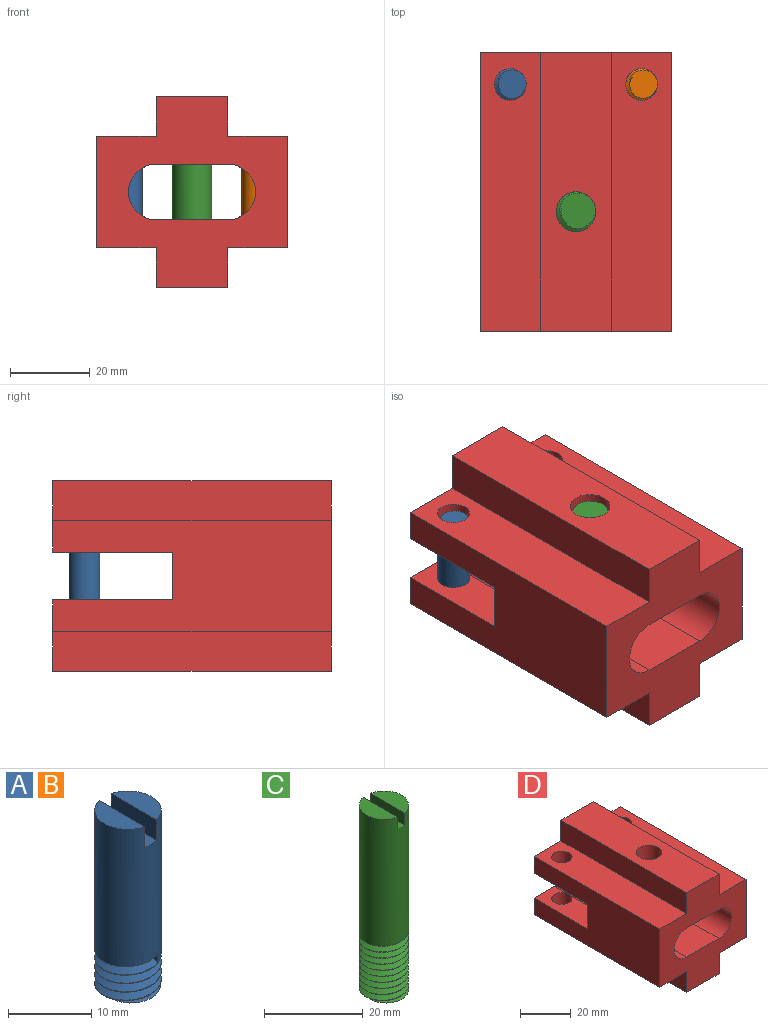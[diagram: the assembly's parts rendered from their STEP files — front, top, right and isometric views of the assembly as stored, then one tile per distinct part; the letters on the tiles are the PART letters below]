
ASSEMBLY  parts=4 mates=3
PART A: 14 faces, bbox 8.7x9.9x27.3 mm
  f0: cylinder r=4mm len=22.25mm, axis (0,0,1), area 508.2mm2, adj f1,f5,f7,f8,f9,f10,f11,f12
  f1: cylinder r=4mm len=8mm, axis (0,0,1), area 2.5mm2, adj f0,f2,f8,f9
  f2: cylinder r=4mm len=8mm, axis (0,0,1), area 2.5mm2, adj f1,f3,f8,f9
  f3: cylinder r=4mm len=8mm, axis (0,0,1), area 2.5mm2, adj f2,f4,f8,f9
  f4: cylinder r=4mm len=1.78mm, axis (0,0,1), area 0.1mm2, adj f3,f6,f9
  f5: plane 7.75x3mm, normal (0,0,1), area 17.2mm2, adj f0,f12
  f6: plane 7.82x7.8mm, normal (0,0,-1), area 39.7mm2, adj f4,f8,f9
  f7: plane 7.75x3mm, normal (0,0,1), area 17.2mm2, adj f0,f11
  f8: bspline ~9.24x8mm, area 116.1mm2, adj f0,f1,f2,f3,f6,f9,f10
  f9: bspline ~8.01x7.99mm, area 104mm2, adj f0,f1,f2,f3,f4,f6,f8,f10
  f10: plane 1.15x0.96mm, normal (-0.95,-0.31,-0.05), area 0.6mm2, adj f0,f8,f9
  f11: plane 7.75x3mm, normal (1,0,0), area 23.2mm2, adj f0,f7,f13
  f12: plane 7.75x3mm, normal (-1,0,0), area 23.2mm2, adj f0,f5,f13
  f13: plane 8x2mm, normal (0,0,1), area 15.8mm2, adj f0,f11,f12
PART B: same geometry as A
PART C: 21 faces, bbox 10.1x11.6x46.8 mm
  f0: cylinder r=5mm len=32.41mm, axis (0,0,1), area 982.6mm2, adj f1,f11,f13,f15,f16,f17,f18,f19
  f1: cylinder r=5mm len=10mm, axis (0,0,1), area 3.1mm2, adj f0,f2,f15,f16
  f2: cylinder r=5mm len=10mm, axis (0,0,1), area 3.1mm2, adj f1,f3,f15,f16
  f3: cylinder r=5mm len=10mm, axis (0,0,1), area 3.1mm2, adj f2,f4,f15,f16
  f4: cylinder r=5mm len=10mm, axis (0,0,1), area 3.1mm2, adj f3,f5,f15,f16
  f5: cylinder r=5mm len=10mm, axis (0,0,1), area 3.1mm2, adj f4,f6,f15,f16
  f6: cylinder r=5mm len=10mm, axis (0,0,1), area 3.1mm2, adj f5,f7,f15,f16
  f7: cylinder r=5mm len=10mm, axis (0,0,1), area 3.1mm2, adj f6,f8,f15,f16
  f8: cylinder r=5mm len=10mm, axis (0,0,1), area 3.1mm2, adj f7,f9,f15,f16
  f9: cylinder r=5mm len=10mm, axis (0,0,1), area 3.1mm2, adj f8,f10,f15,f16
  f10: cylinder r=5mm len=3.46mm, axis (0,0,1), area 0.4mm2, adj f9,f12,f14,f15,f16
  f11: plane 9.8x4mm, normal (0,0,1), area 29.3mm2, adj f0,f19
  f12: plane 9.05x8.93mm, normal (0,0,-1), area 62.4mm2, adj f10,f14,f15,f16
  f13: plane 9.8x4mm, normal (0,0,1), area 29.3mm2, adj f0,f18
  f14: plane 0.15x0.09mm, normal (0,1,0.05), area 0mm2, adj f10,f12,f15
  f15: bspline ~15.7x9.99mm, area 380.5mm2, adj f0,f1,f2,f3,f4,f5,f6,f7
  f16: bspline ~15.2x11.55mm, area 362mm2, adj f0,f1,f2,f3,f4,f5,f6,f7
  f17: plane 1.4x1.21mm, normal (0,-1,-0.05), area 0.8mm2, adj f0,f15,f16
  f18: plane 9.8x3mm, normal (1,0,0), area 29.4mm2, adj f0,f13,f20
  f19: plane 9.8x3mm, normal (-1,0,0), area 29.4mm2, adj f0,f11,f20
  f20: plane 10x2mm, normal (0,0,1), area 19.9mm2, adj f0,f18,f19
PART D: 31 faces, bbox 48x70x48 mm
  f0: plane 48x18mm, normal (0,1,0), area 541.1mm2, adj f1,f2,f3,f9,f10,f11,f12,f13
  f1: plane 70x28mm, normal (1,0,0), area 1600mm2, adj f0,f4,f5,f14,f15,f22,f23,f24
  f2: cylinder r=7mm len=70mm, axis (0,1,0), area 1106.6mm2, adj f0,f4,f5,f17,f18,f22,f23,f24
  f3: cylinder r=7mm len=70mm, axis (0,1,0), area 1106.6mm2, adj f0,f4,f5,f17,f18,f19,f20,f21
  f4: plane 48x48mm, normal (0,-1,0), area 1298.1mm2, adj f1,f2,f3,f6,f7,f8,f9,f10
  f5: plane 48x18mm, normal (0,1,0), area 541.1mm2, adj f1,f2,f3,f6,f7,f8,f9,f15
  f6: plane 70x18mm, normal (0,0,1), area 1181.5mm2, adj f4,f5,f7,f16,f30
  f7: plane 70x10mm, normal (-1,0,0), area 700mm2, adj f4,f5,f6,f8
  f8: plane 70x15mm, normal (0,0,1), area 999.7mm2, adj f4,f5,f7,f9,f27
  f9: plane 70x28mm, normal (-1,0,0), area 1600mm2, adj f0,f4,f5,f8,f10,f19,f20,f21
  f10: plane 70x15mm, normal (0,0,-1), area 999.7mm2, adj f0,f4,f9,f11,f28
  f11: plane 70x10mm, normal (-1,0,0), area 700mm2, adj f0,f4,f10,f12
  f12: plane 70x18mm, normal (0,0,-1), area 1181.5mm2, adj f0,f4,f11,f13,f29
  f13: plane 70x10mm, normal (1,0,0), area 700mm2, adj f0,f4,f12,f14
  f14: plane 70x15mm, normal (0,0,-1), area 999.7mm2, adj f0,f1,f4,f13,f25
  f15: plane 70x15mm, normal (0,0,1), area 999.7mm2, adj f1,f4,f5,f16,f26
  f16: plane 70x10mm, normal (1,0,0), area 700mm2, adj f4,f5,f6,f15
  f17: plane 70x18mm, normal (0,0,-1), area 1181.5mm2, adj f2,f3,f4,f5,f30
  f18: plane 70x18mm, normal (0,0,1), area 1181.5mm2, adj f0,f2,f3,f4,f29
  f19: plane 12x11.39mm, normal (0,1,0), area 107.9mm2, adj f3,f9,f20,f21
  f20: plane 30x11.39mm, normal (0,0,1), area 291.7mm2, adj f0,f3,f9,f19,f28
  f21: plane 30x11.39mm, normal (0,0,-1), area 291.7mm2, adj f3,f5,f9,f19,f27
  f22: plane 30x11.39mm, normal (0,0,-1), area 291.7mm2, adj f1,f2,f5,f24,f26
  f23: plane 30x11.39mm, normal (0,0,1), area 291.7mm2, adj f0,f1,f2,f24,f25
  f24: plane 12x11.39mm, normal (0,1,0), area 107.9mm2, adj f1,f2,f22,f23
  f25: cylinder r=4mm len=8mm, axis (0,0,-1), area 201mm2, adj f2,f14,f23
  f26: cylinder r=4mm len=8mm, axis (0,0,-1), area 201mm2, adj f2,f15,f22
  f27: cylinder r=4mm len=8mm, axis (0,0,-1), area 201mm2, adj f3,f8,f21
  f28: cylinder r=4mm len=8mm, axis (0,0,-1), area 201mm2, adj f3,f10,f20
  f29: cylinder r=5mm len=17mm, axis (0,0,-1), area 534.1mm2, adj f12,f18
  f30: cylinder r=5mm len=17mm, axis (0,0,-1), area 534.1mm2, adj f6,f17
PLACE A rot(axis=(1,0,0),180deg) t=(33.95,42.84,51.83)mm
PLACE B rot(axis=(1,0,0),180deg) t=(66.95,42.84,51.83)mm
PLACE C rot(axis=(1,0,0),180deg) t=(25.99,30.44,52.83)mm
PLACE D t=(4.44,-3.17,45.83)mm
MATE fastened B.f0 <-> D.f25  axis (0,0,-1) through (20.94,-11.17,31.83)mm
MATE fastened A.f0 <-> D.f27  axis (0,0,-1) through (-12.06,-11.17,31.83)mm
MATE fastened C.f0 <-> D.f29  axis (0,0,-1) through (4.44,-43.17,21.83)mm
